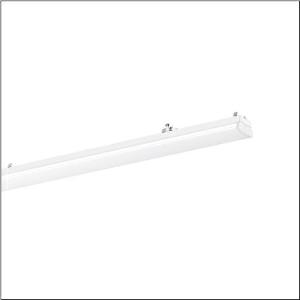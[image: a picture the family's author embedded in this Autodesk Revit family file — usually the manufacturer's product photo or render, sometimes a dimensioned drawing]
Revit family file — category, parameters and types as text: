
# Revit family: licross_r__21_recessed_opal_mo_52tl1d7n46xg_6fbc
name_source: partatom
category: Lighting Fixtures
units: mm (PartAtom-declared; Revit-internal decimal feet)

## family parameters
Cut with Voids When Loaded = No
Host = Face
Light Source = No
Part Type = Normal
Room Calculation Point = No
Round Connector Dimension = Use Diameter
Shared = No

## types (1)
- Licross® 21 recessed opal MO (1 x LED, 6200 lm, 34.9 W, 4000K)
    Apparent Load = 35 VA
    CIE Flux Codes = 44 73 91 87 100
    Color Rendering = 80
    Color Temperature = 4000K
    Default Elevation = 1800 mm
    Description = Licross® 21 recessed opal MO, luminaire insert, of sheet steel, galvanised, coil coated, white, length: 1.500mm, width: 66mm, height: 67mm, LED rated luminous flux: 6.200lm, light colour: 840, control gear: ON/OFF, with plug, 3-pole, with phase selection, mains connection: 220..240V, AC, 50/60Hz, rated input power: 35W, halogen-free wiring, primary optical cover: cover, of PMMA, light emission: direct with ceiling illumination distribution, primary light characteristic: symmetric, protection rating (complete): IP40, insulation class (complete): insulation class I (protective earthing), certification: CE, ENEC, VDE, UKCA, protection symbol: D if used in an environment without relevant dust loads with corresponding accessories, impact resistance: IK06, permissible ambient temperature for indoor applications: -35..+50°C, corresponds to IFS (International Featured Standards) requirements for safety and quality in the food industry, reducing of maximum allowable ambient temperature of 5°C with ceiling mounting, LABS conformity tested according to VDMA 24364:2018-05, packaging unit: 1 piece
    Height = 83 mm
    Lamp = 1 x LED
    Lamp Light Flux = 6200 lm
    Lamp Power = 34.9 W
    Lamp count = 1
    Length = 1500 mm
    Luminous efficacy = 178 lm/W
    Manufacturer = Siteco
    ModVariant = No
    Model = 52TL1D7N46XG
    Mounting Place = Ceiling
    Mounting Type = Pendant
    Number of Poles = 1
    OnlyDefault = Yes
    Power Factor = 1
    Product Name = Licross® 21 recessed opal MO
    Product group = luminaire insert
    ProductGroupID = 901
    Protection Class = Protection class I
    Protection Degree = IP 40
    RLX_Detail_Level = 1
    RLX_Emergency_Light_Flux = 0 lm
    RLX_Emergency_Type = 0
    RLX_Emergency_Type_DB = No
    RlxData = <blob elided: 23061 chars, md5=0a39c71f>
    Socket = socket
    Standby Power = 0 W
    System Light Flux = 6200 lm
    System Power = 35 W
    Type Comments = Product without accessories
    Type Image = l_1313666.jpg
    URL = http://relux.com
    VarID = ---
    Voltage = 0 V
    Weight = 0.00 kg
    Width = 76 mm

## geometry (parser evidence)
native form markers: Blend x4, Sweep x13
no freeform markers — native parametric forms only
